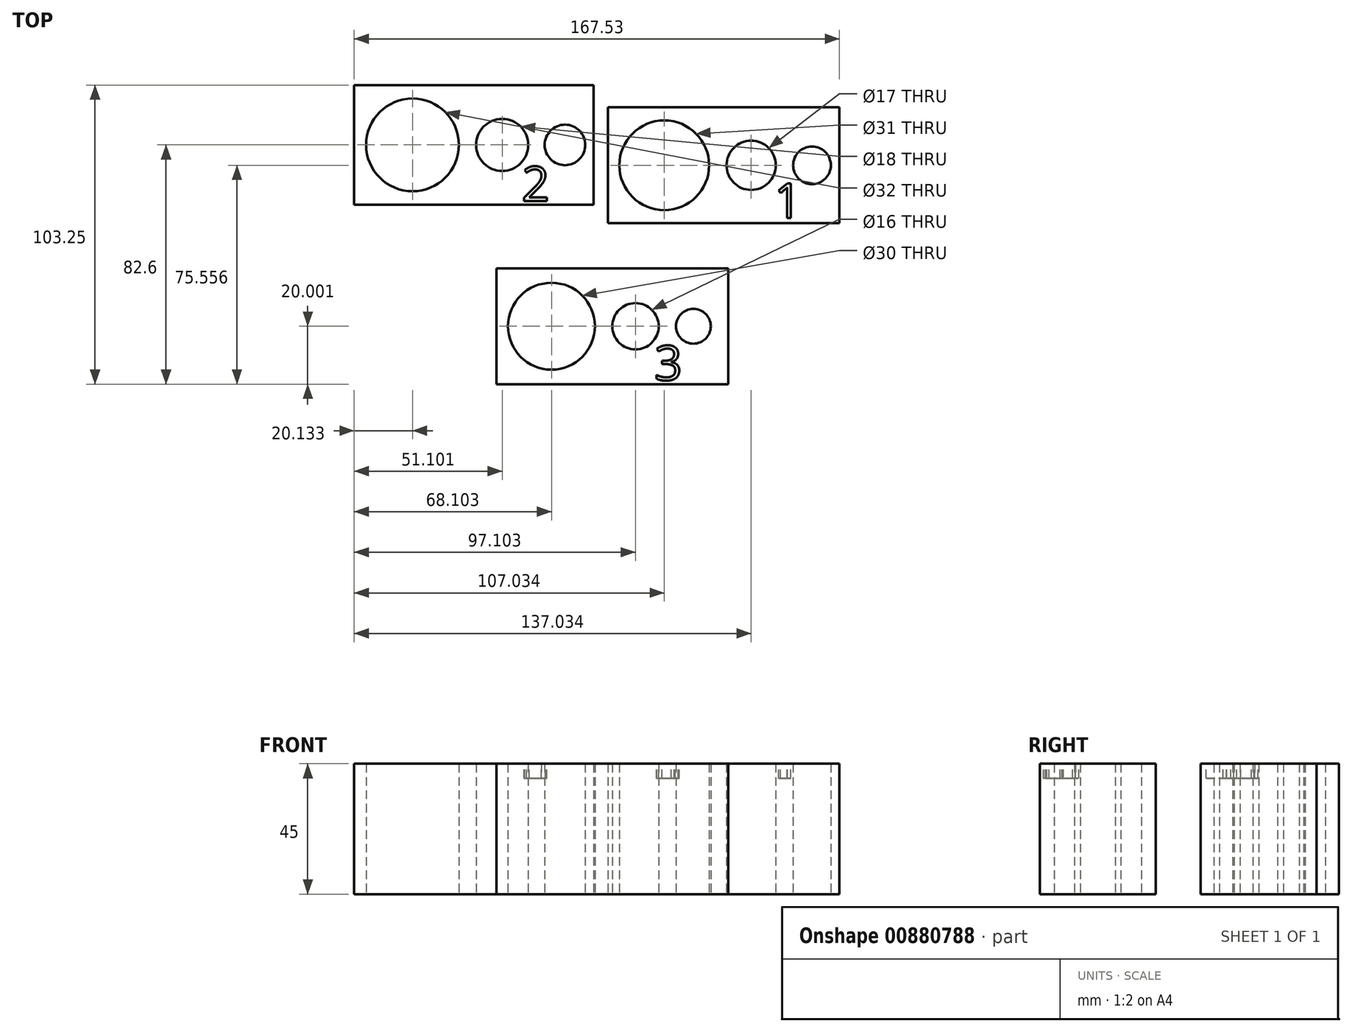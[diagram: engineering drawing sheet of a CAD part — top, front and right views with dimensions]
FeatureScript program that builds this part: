
annotation { "Feature Type Name" : "Feature", "Feature Type Description" : "" }
export const myFeature = defineFeature(function(context is Context, id is Id, definition is map)
    precondition{}
    {
        {
            var Q0;
            Q0=qCreatedBy(makeId("Top.planeOp"),FACE);
            var sketch = newSketch(context, id + "F0", { "sketchPlane" : qUnion([Q0])});
            skLineSegment(sketch, "E0", {"start": v(-0.25, 41.16) * mm, "end": v(79.75, 41.16) * mm});
            skLineSegment(sketch, "E1", {"start": v(79.75, 41.16) * mm, "end": v(79.75, 1.16) * mm});
            skLineSegment(sketch, "E2", {"start": v(79.75, 1.16) * mm, "end": v(-0.25, 1.16) * mm});
            skLineSegment(sketch, "E3", {"start": v(-0.25, 1.16) * mm, "end": v(-0.25, 41.16) * mm});
            skCircle(sketch, "E4", {"center": v(19.25, 21.16) * mm, "radius": 15.5 * mm});
            skCircle(sketch, "E5", {"center": v(49.25, 21.16) * mm, "radius": 8.5 * mm});
            skCircle(sketch, "E6", {"center": v(70.25, 21.16) * mm, "radius": 6.5 * mm});
            skSolve(sketch);
        }
        {
            var Q0;
            Q0=qCreatedBy(makeId("Top.planeOp"),FACE);
            var sketch = newSketch(context, id + "F1", { "sketchPlane" : qUnion([Q0])});
            skLineSegment(sketch, "E7", {"start": v(-87.78, 48.85) * mm, "end": v(-5.2, 48.85) * mm});
            skLineSegment(sketch, "E8", {"start": v(-5.2, 48.85) * mm, "end": v(-5.2, 7.55) * mm});
            skLineSegment(sketch, "E9", {"start": v(-5.2, 7.55) * mm, "end": v(-87.78, 7.55) * mm});
            skLineSegment(sketch, "E10", {"start": v(-87.78, 7.55) * mm, "end": v(-87.78, 48.85) * mm});
            skCircle(sketch, "E11", {"center": v(-67.65, 28.2) * mm, "radius": 16 * mm});
            skCircle(sketch, "E12", {"center": v(-36.68, 28.2) * mm, "radius": 9 * mm});
            skCircle(sketch, "E13", {"center": v(-15, 28.2) * mm, "radius": 7 * mm});
            skSolve(sketch);
        }
        {
            var Q0;
            Q0=qCreatedBy(makeId("Top.planeOp"),FACE);
            var sketch = newSketch(context, id + "F2", { "sketchPlane" : qUnion([Q0])});
            skLineSegment(sketch, "E14", {"start": v(-38.68, -14.4) * mm, "end": v(41.32, -14.4) * mm});
            skLineSegment(sketch, "E15", {"start": v(41.32, -14.4) * mm, "end": v(41.32, -54.4) * mm});
            skLineSegment(sketch, "E16", {"start": v(41.32, -54.4) * mm, "end": v(-38.68, -54.4) * mm});
            skLineSegment(sketch, "E17", {"start": v(-38.68, -54.4) * mm, "end": v(-38.68, -14.4) * mm});
            skCircle(sketch, "E18", {"center": v(-19.68, -34.4) * mm, "radius": 15 * mm});
            skCircle(sketch, "E19", {"center": v(9.32, -34.4) * mm, "radius": 8 * mm});
            skCircle(sketch, "E20", {"center": v(29.32, -34.4) * mm, "radius": 6 * mm});
            skSolve(sketch);
        }
        {
            var Q0;
            Q0=makeQuery(id+"F1.imprint","IMPRINT",FACE,{"disambiguationData":[TD([[makeQuery(id+"F1.imprint","IMPRINT",EDGE,{"derivedFrom":sQuery(id+"F1.wireOp",EDGE,"E7")}),-1.0]])]});
            var Q1;
            Q1=makeQuery(id+"F0.imprint","IMPRINT",FACE,{"disambiguationData":[TD([[makeQuery(id+"F0.imprint","IMPRINT",EDGE,{"derivedFrom":sQuery(id+"F0.wireOp",EDGE,"E0")}),-1.0]])]});
            var Q2;
            Q2=makeQuery(id+"F2.imprint","IMPRINT",FACE,{"disambiguationData":[TD([[makeQuery(id+"F2.imprint","IMPRINT",EDGE,{"derivedFrom":sQuery(id+"F2.wireOp",EDGE,"E14")}),-1.0]])]});
            extrude(context, id + "F3", {"entities" : qUnion([Q0, Q1, Q2]), "depth" : 45 * mm, "offsetDistance" : 25 * mm});
        }
        {
            var Q0;
            Q0=makeQuery(id+"F3.opExtrude","CAP_FACE",FACE,{"disambiguationData":[OSD([sQuery(id+"F1.wireOp",EDGE,"E7"),sQuery(id+"F1.wireOp",EDGE,"E8"),sQuery(id+"F1.wireOp",EDGE,"E9"),sQuery(id+"F1.wireOp",EDGE,"E10"),sQuery(id+"F1.wireOp",EDGE,"E11"),sQuery(id+"F1.wireOp",EDGE,"E12"),sQuery(id+"F1.wireOp",EDGE,"E13")])],"isStart":false});
            var sketch = newSketch(context, id + "F4", { "sketchPlane" : qUnion([Q0])});
            skText(sketch, "E21", { "text": "1", "fontName": "OpenSans-Regular.ttf"});
            skText(sketch, "E22", { "text": "2", "fontName": "OpenSans-Regular.ttf"});
            skText(sketch, "E23", { "text": "3", "fontName": "OpenSans-Regular.ttf"});
            const initialGuessF4  = {"E21": [0.05716, 0.00303, 1, 0, 0.012], "E22": [-0.0299, 0.00882, 1, 0, 0.012], "E23": [0.01588, -0.05302, 1, 0, 0.012]};
            skSetInitialGuess(sketch, initialGuessF4);
            skSolve(sketch);
        }
        {
            var Q0;
            Q0 = qSketchRegion(id + "F4", true);
            extrude(context, id + "F5", {"entities" : qUnion([Q0]), "operationType" : NewBodyOperationType.REMOVE, "oppositeDirection" : true, "depth" : 5 * mm, "offsetDistance" : 25 * mm});
        }
    });
